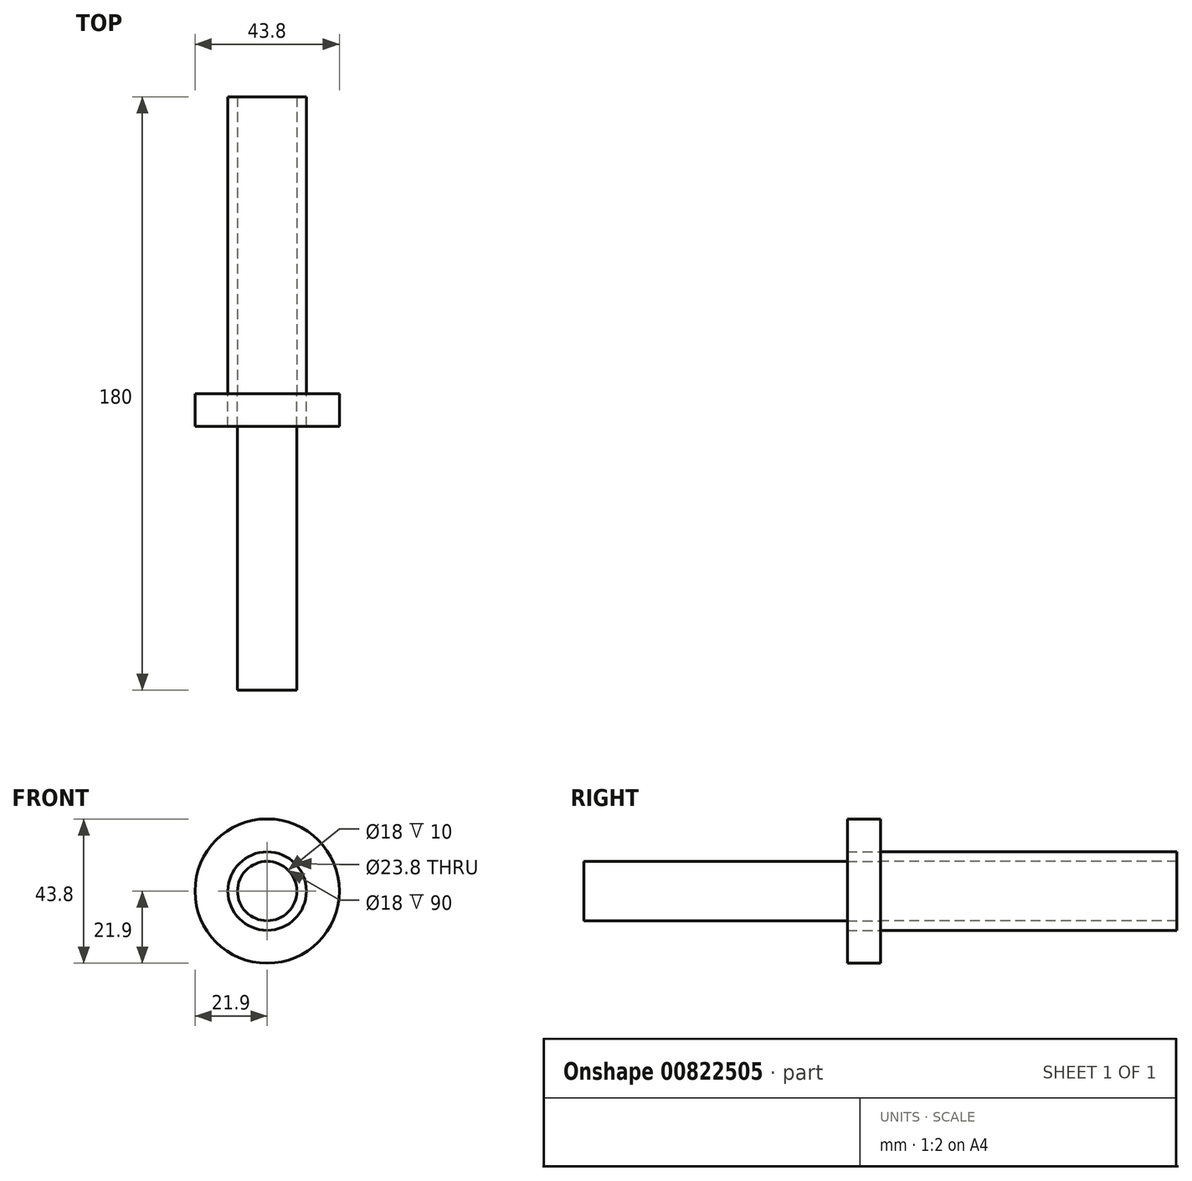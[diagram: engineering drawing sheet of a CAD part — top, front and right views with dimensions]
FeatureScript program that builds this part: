
annotation { "Feature Type Name" : "Feature", "Feature Type Description" : "" }
export const myFeature = defineFeature(function(context is Context, id is Id, definition is map)
    precondition{}
    {
        {
            var Q0;
            Q0=qCreatedBy(makeId("Front.planeOp"),FACE);
            var sketch = newSketch(context, id + "F0", { "sketchPlane" : qUnion([Q0])});
            skCircle(sketch, "E0", {"center": v(0, 0) * mm, "radius": 9 * mm});
            skCircle(sketch, "E1", {"center": v(0, 0) * mm, "radius": 11.9 * mm});
            skCircle(sketch, "E2", {"center": v(0, 0) * mm, "radius": 21.9 * mm});
            skSolve(sketch);
        }
        {
            var Q0;
            Q0=makeQuery(id+"F0.imprint","IMPRINT",FACE,{"disambiguationData":[TD([[makeQuery(id+"F0.imprint","IMPRINT",EDGE,{"derivedFrom":sQuery(id+"F0.wireOp",EDGE,"E0")}),1.0]])]});
            extrude(context, id + "F1", {"entities" : qUnion([Q0]), "depth" : 90 * mm, "offsetDistance" : 25 * mm});
        }
        {
            var Q0;
            Q0=makeQuery(id+"F0.imprint","IMPRINT",FACE,{"disambiguationData":[TD([[makeQuery(id+"F0.imprint","IMPRINT",EDGE,{"derivedFrom":sQuery(id+"F0.wireOp",EDGE,"E1")}),-1.0]])]});
            extrude(context, id + "F2", {"entities" : qUnion([Q0]), "depth" : 10 * mm, "offsetDistance" : 25 * mm});
        }
        {
            var Q0;
            Q0=makeQuery(id+"F0.imprint","IMPRINT",FACE,{"disambiguationData":[TD([[makeQuery(id+"F0.imprint","IMPRINT",EDGE,{"derivedFrom":sQuery(id+"F0.wireOp",EDGE,"E0")}),-1.0]])]});
            extrude(context, id + "F3", {"entities" : qUnion([Q0]), "oppositeDirection" : true, "depth" : 90 * mm, "offsetDistance" : 25 * mm});
        }
        {
            var Q0;
            Q0=makeQuery(id+"F0.imprint","IMPRINT",FACE,{"disambiguationData":[TD([[makeQuery(id+"F0.imprint","IMPRINT",EDGE,{"derivedFrom":sQuery(id+"F0.wireOp",EDGE,"E0")}),-1.0]])]});
            extrude(context, id + "F4", {"entities" : qUnion([Q0]), "depth" : 10 * mm, "offsetDistance" : 25 * mm});
        }
        {
            var Q0;
            Q0=makeQuery(id+"F1.opExtrude","CAP_FACE",FACE,{"disambiguationData":[OSD([sQuery(id+"F0.wireOp",EDGE,"E0")])],"isStart":true});
            extrude(context, id + "F5", {"entities" : qUnion([Q0]), "depth" : 90 * mm, "offsetDistance" : 25 * mm});
        }
    });
